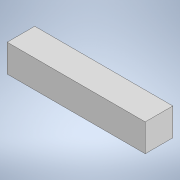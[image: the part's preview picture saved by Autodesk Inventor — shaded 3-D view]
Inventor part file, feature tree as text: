
AUTODESK INVENTOR PART (.ipt)
format: ipt  version: 2022 (Build 260153070, 153G)  size: 89,600 bytes
history: native  units: in
note: dims shown in document units (in); Inventor stores cm internally (conversion verified against a paired STEP export)
features: extrude x1, sketch x1
ambient origin geometry x8: Origin, YZ Plane, XZ Plane, XY Plane, X Axis, Y Axis, Z Axis, Center Point
bodies: Solid1 (feature_tree)
feature tree (2):
  extrude  "Extrusion1"  Depth=2.0in
  sketch  "Sketch1"  dims[d0=10.0in d1=2.0in d2=2.0in d3=0.0in]
